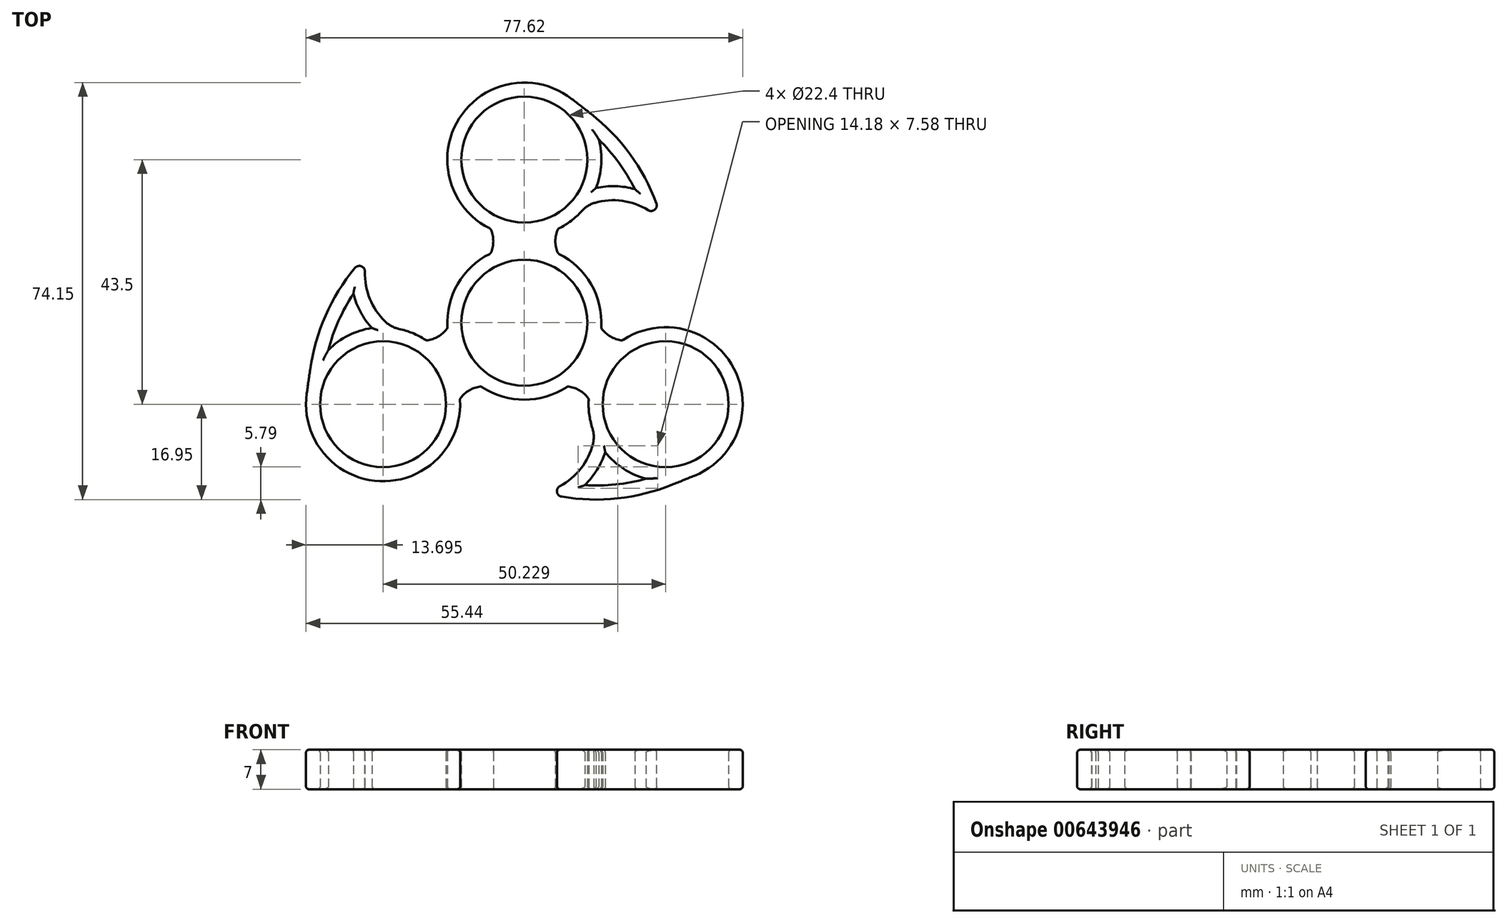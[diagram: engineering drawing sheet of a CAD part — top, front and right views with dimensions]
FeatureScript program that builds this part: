
annotation { "Feature Type Name" : "Feature", "Feature Type Description" : "" }
export const myFeature = defineFeature(function(context is Context, id is Id, definition is map)
    precondition{}
    {
        {
            var Q0;
            Q0=qCreatedBy(makeId("Top.planeOp"),FACE);
            var sketch = newSketch(context, id + "F0", { "sketchPlane" : qUnion([Q0])});
            skCircle(sketch, "E0", {"center": v(0, 0) * mm, "radius": 11.2 * mm});
            skLineSegment(sketch, "E1", {"start": v(0, 0) * mm, "end": v(0, 29) * mm, "construction": true});
            skCircle(sketch, "E2", {"center": v(0, 29) * mm, "radius": 11.2 * mm});
            skLineSegment(sketch, "E3", {"start": v(-11.2, 0) * mm, "end": v(11.2, 0) * mm, "construction": true});
            skLineSegment(sketch, "E4", {"start": v(-11.2, 29) * mm, "end": v(11.2, 29) * mm, "construction": true});
            skArc(sketch, "E5.0", {"start": v(-6, 12.32) * mm, "mid": v(0, -13.7) * mm, "end": v(6, 12.32) * mm});
            skLineSegment(sketch, "E6", {"start": v(0, 42.7) * mm, "end": v(0, 15.3) * mm, "construction": true});
            skLineSegment(sketch, "E7.0", {"start": v(6, 9.46) * mm, "end": v(6, 19.54) * mm, "construction": true});
            skArc(sketch, "E8", {"start": v(6, 16.68) * mm, "mid": v(5.52, 14.5) * mm, "end": v(6, 12.32) * mm});
            skArc(sketch, "E9.MirrorCS", {"start": v(-6, 16.68) * mm, "mid": v(-5.52, 14.5) * mm, "end": v(-6, 12.32) * mm});
            skArc(sketch, "E10.trimOffspring", {"start": v(6, 16.68) * mm, "mid": v(8.7, 18.4) * mm, "end": v(10.9, 20.71) * mm});
            skArc(sketch, "E11", {"start": v(24.52, 17.91) * mm, "mid": v(19, 29.66) * mm, "end": v(9.67, 38.7) * mm});
            skArc(sketch, "E12", {"start": v(24.52, 17.91) * mm, "mid": v(18.17, 21.54) * mm, "end": v(10.9, 20.71) * mm});
            skArc(sketch, "E13.0", {"start": v(19.65, 23.75) * mm, "mid": v(16.2, 24.27) * mm, "end": v(12.73, 23.95) * mm});
            skArc(sketch, "E13.1", {"start": v(19.65, 23.75) * mm, "mid": v(16.8, 28.44) * mm, "end": v(13.22, 32.6) * mm});
            skArc(sketch, "E14.trimOffspring", {"start": v(9.67, 38.7) * mm, "mid": v(-11.16, 36.94) * mm, "end": v(-6, 16.68) * mm});
            skArc(sketch, "E15.trimOffspring", {"start": v(12.73, 23.95) * mm, "mid": v(13.68, 28.23) * mm, "end": v(13.22, 32.6) * mm});
            skSolve(sketch);
        }
        {
            var Q0;
            Q0=makeQuery(id+"F0.imprint","IMPRINT",FACE,{"disambiguationData":[TD([[makeQuery(id+"F0.imprint","IMPRINT",EDGE,{"derivedFrom":sQuery(id+"F0.wireOp",EDGE,"E0")}),-1.0]])]});
            extrude(context, id + "F1", {"entities" : qUnion([Q0]), "depth" : 7 * mm, "offsetDistance" : 25 * mm});
        }
        {
            var Q0;
            Q0=qCreatedBy(makeId("Right.planeOp"),FACE);
            var sketch = newSketch(context, id + "F2", { "sketchPlane" : qUnion([Q0])});
            skLineSegment(sketch, "E16", {"start": v(0, 0) * mm, "end": v(0, 24.15) * mm, "construction": true});
            skSolve(sketch);
        }
        {
            var Q0;
            Q0=makeQuery(id+"F1.opExtrude","SWEPT_EDGE",EDGE,{"disambiguationData":[OSD([sQuery(id+"F0.wireOp",EDGE,"E11"),sQuery(id+"F0.wireOp",EDGE,"E12")])]});
            fillet(context, id + "F3", {"entities" : qUnion([Q0]), "radius" : 1 * mm, "tangentPropagation" : true, "allowEdgeOverflow" : false});
        }
        {
            var Q0;
            Q0=makeQuery(id+"F1.opExtrude","SWEPT_EDGE",EDGE,{"disambiguationData":[OSD([sQuery(id+"F0.wireOp",EDGE,"E10.trimOffspring"),sQuery(id+"F0.wireOp",EDGE,"E12")])]});
            fillet(context, id + "F4", {"entities" : qUnion([Q0]), "radius" : 5 * mm, "tangentPropagation" : true, "allowEdgeOverflow" : false});
        }
        {
            var Q0;
            Q0=makeQuery(id+"F1.opExtrude","SWEPT_EDGE",EDGE,{"disambiguationData":[OSD([sQuery(id+"F0.wireOp",EDGE,"E8"),sQuery(id+"F0.wireOp",EDGE,"a7715e3d-49e1-4b64-8228-6264ce36ffdd.trimOffspring")])]});
            var Q1;
            Q1=makeQuery(id+"F1.opExtrude","SWEPT_EDGE",EDGE,{"disambiguationData":[OSD([sQuery(id+"F0.wireOp",EDGE,"vL0yK9kr-aUAw-fq5m-LhdP-4na97wzfjfiJ"),sQuery(id+"F0.wireOp",EDGE,"a7715e3d-49e1-4b64-8228-6264ce36ffdd.trimOffspring")])]});
            var Q2;
            Q2=makeQuery(id+"F1.opExtrude","SWEPT_EDGE",EDGE,{"disambiguationData":[OSD([sQuery(id+"F0.wireOp",EDGE,"0uLAjghk-3gFu-Hscj-w9fE-ttjJYeJmuMDI"),sQuery(id+"F0.wireOp",EDGE,"vL0yK9kr-aUAw-fq5m-LhdP-4na97wzfjfiJ")])]});
            var Q3;
            Q3=makeQuery(id+"F1.opExtrude","SWEPT_EDGE",EDGE,{"disambiguationData":[OSD([sQuery(id+"F0.wireOp",EDGE,"59cc2289-ca77-47a6-96da-44b8b7f5bab30.MirrorCS"),sQuery(id+"F0.wireOp",EDGE,"5cff57ee-30ec-4a3f-ae05-e4d68d5af566.0")])]});
            var Q4;
            Q4=makeQuery(id+"F1.opExtrude","SWEPT_EDGE",EDGE,{"disambiguationData":[OSD([sQuery(id+"F0.wireOp",EDGE,"Nf5N08YX-LUpC-YIFK-iieG-ll9huf0In2a7"),sQuery(id+"F0.wireOp",EDGE,"59cc2289-ca77-47a6-96da-44b8b7f5bab30.MirrorCS")])]});
            var Q5;
            Q5=makeQuery(id+"F1.opExtrude","SWEPT_EDGE",EDGE,{"disambiguationData":[OSD([sQuery(id+"F0.wireOp",EDGE,"Nf5N08YX-LUpC-YIFK-iieG-ll9huf0In2a7"),sQuery(id+"F0.wireOp",EDGE,"8e5a45cd-34c5-40eb-b1f5-600c90d6d9e0.0")])]});
            var Q6;
            Q6=makeQuery(id+"F1.opExtrude","SWEPT_EDGE",EDGE,{"disambiguationData":[OSD([sQuery(id+"F0.wireOp",EDGE,"8e5a45cd-34c5-40eb-b1f5-600c90d6d9e0.0"),sQuery(id+"F0.wireOp",EDGE,"5cff57ee-30ec-4a3f-ae05-e4d68d5af566.0")])]});
            var Q7;
            Q7=makeQuery(id+"F1.opExtrude","SWEPT_EDGE",EDGE,{"disambiguationData":[OSD([sQuery(id+"F0.wireOp",EDGE,"E9.MirrorCS"),sQuery(id+"F0.wireOp",EDGE,"E14.trimOffspring")])]});
            var Q8;
            Q8=makeQuery(id+"F1.opExtrude","SWEPT_EDGE",EDGE,{"disambiguationData":[OSD([sQuery(id+"F0.wireOp",EDGE,"E5.0"),sQuery(id+"F0.wireOp",EDGE,"E9.MirrorCS")])]});
            fillet(context, id + "F5", {"entities" : qUnion([Q0, Q1, Q2, Q3, Q4, Q5, Q6, Q7, Q8]), "radius" : 0.5 * mm, "tangentPropagation" : true, "allowEdgeOverflow" : false});
        }
        {
            var Q0;
            Q0=makeQuery(id+"F1.opExtrude","SWEPT_EDGE",EDGE,{"disambiguationData":[OSD([sQuery(id+"F0.wireOp",EDGE,"E11"),sQuery(id+"F0.wireOp",EDGE,"E14.trimOffspring")])]});
            fillet(context, id + "F6", {"entities" : qUnion([Q0]), "radius" : 1952.43 * mm, "tangentPropagation" : true, "allowEdgeOverflow" : false});
        }
        {
            var Q0;
            Q0=makeQuery(id+"F1.opExtrude","SWEPT_BODY",BODY,{"disambiguationData":[OSD([sQuery(id+"F0.wireOp",EDGE,"E0"),sQuery(id+"F0.wireOp",EDGE,"E2"),sQuery(id+"F0.wireOp",EDGE,"E5.0"),sQuery(id+"F0.wireOp",EDGE,"beef2716-db7f-41ab-9648-4623db96a248.0"),sQuery(id+"F0.wireOp",EDGE,"0uLAjghk-3gFu-Hscj-w9fE-ttjJYeJmuMDI"),sQuery(id+"F0.wireOp",EDGE,"vL0yK9kr-aUAw-fq5m-LhdP-4na97wzfjfiJ"),sQuery(id+"F0.wireOp",EDGE,"c7e23209-4e23-4cac-a964-1c74d8cbfa74.0"),sQuery(id+"F0.wireOp",EDGE,"c7e23209-4e23-4cac-a964-1c74d8cbfa74.1"),sQuery(id+"F0.wireOp",EDGE,"df6599d3-b23b-4a78-9647-52215b223935.trimOffspring"),sQuery(id+"F0.wireOp",EDGE,"E8"),sQuery(id+"F0.wireOp",EDGE,"E9.MirrorCS"),sQuery(id+"F0.wireOp",EDGE,"7884432a-9f31-4921-b3fb-1dd42b4fd2c3.0"),sQuery(id+"F0.wireOp",EDGE,"36360b40-f322-41f0-b5ba-529e4c97dfdc.0"),sQuery(id+"F0.wireOp",EDGE,"c7395060-edcf-4106-a591-bdadd866a779.0"),sQuery(id+"F0.wireOp",EDGE,"68ec89d5-ddd9-4a57-ad5e-668f128be303.0"),sQuery(id+"F0.wireOp",EDGE,"a7715e3d-49e1-4b64-8228-6264ce36ffdd.trimOffspring")])]});
            var Q1;
            Q1=sQuery(id+"F2.wireOp",EDGE,"E16");
            circularPattern(context, id + "F7", {"operationType" : NewBodyOperationType.ADD, "entities" : qUnion([Q0]), "axis" : qUnion([Q1]), "angle" : 360 * degree, "instanceCount" : 3, "equalSpace" : true});
        }
        {
            var Q0;
            {var subQ0=makeQuery(id+"F1.opExtrude","CAP_FACE",FACE,{"disambiguationData":[OSD([sQuery(id+"F0.wireOp",EDGE,"E0"),sQuery(id+"F0.wireOp",EDGE,"E2"),sQuery(id+"F0.wireOp",EDGE,"E5.0"),sQuery(id+"F0.wireOp",EDGE,"E8"),sQuery(id+"F0.wireOp",EDGE,"E9.MirrorCS"),sQuery(id+"F0.wireOp",EDGE,"Nf5N08YX-LUpC-YIFK-iieG-ll9huf0In2a7"),sQuery(id+"F0.wireOp",EDGE,"8e5a45cd-34c5-40eb-b1f5-600c90d6d9e0.0"),sQuery(id+"F0.wireOp",EDGE,"59cc2289-ca77-47a6-96da-44b8b7f5bab30.MirrorCS"),sQuery(id+"F0.wireOp",EDGE,"5cff57ee-30ec-4a3f-ae05-e4d68d5af566.0"),sQuery(id+"F0.wireOp",EDGE,"E10.trimOffspring"),sQuery(id+"F0.wireOp",EDGE,"E11"),sQuery(id+"F0.wireOp",EDGE,"E12"),sQuery(id+"F0.wireOp",EDGE,"E13.0"),sQuery(id+"F0.wireOp",EDGE,"E13.1"),sQuery(id+"F0.wireOp",EDGE,"E14.trimOffspring"),sQuery(id+"F0.wireOp",EDGE,"E15.trimOffspring")])],"isStart":false});Q0=makeQuery(id+"F7.boolean.opBoolean","MERGE",FACE,{"derivedFrom":[subQ0,makeQuery(id+"F7.opPattern","COPY",FACE,{"derivedFrom":subQ0,"instanceName":"1"}),makeQuery(id+"F7.opPattern","COPY",FACE,{"derivedFrom":subQ0,"instanceName":"2"})]});}
            var Q1;
            {var subQ0=makeQuery(id+"F1.opExtrude","CAP_FACE",FACE,{"disambiguationData":[OSD([sQuery(id+"F0.wireOp",EDGE,"E0"),sQuery(id+"F0.wireOp",EDGE,"E2"),sQuery(id+"F0.wireOp",EDGE,"E5.0"),sQuery(id+"F0.wireOp",EDGE,"E8"),sQuery(id+"F0.wireOp",EDGE,"E9.MirrorCS"),sQuery(id+"F0.wireOp",EDGE,"Nf5N08YX-LUpC-YIFK-iieG-ll9huf0In2a7"),sQuery(id+"F0.wireOp",EDGE,"8e5a45cd-34c5-40eb-b1f5-600c90d6d9e0.0"),sQuery(id+"F0.wireOp",EDGE,"59cc2289-ca77-47a6-96da-44b8b7f5bab30.MirrorCS"),sQuery(id+"F0.wireOp",EDGE,"5cff57ee-30ec-4a3f-ae05-e4d68d5af566.0"),sQuery(id+"F0.wireOp",EDGE,"E10.trimOffspring"),sQuery(id+"F0.wireOp",EDGE,"E11"),sQuery(id+"F0.wireOp",EDGE,"E12"),sQuery(id+"F0.wireOp",EDGE,"E13.0"),sQuery(id+"F0.wireOp",EDGE,"E13.1"),sQuery(id+"F0.wireOp",EDGE,"E14.trimOffspring"),sQuery(id+"F0.wireOp",EDGE,"E15.trimOffspring")])],"isStart":true});Q1=makeQuery(id+"F7.boolean.opBoolean","MERGE",FACE,{"derivedFrom":[subQ0,makeQuery(id+"F7.opPattern","COPY",FACE,{"derivedFrom":subQ0,"instanceName":"1"}),makeQuery(id+"F7.opPattern","COPY",FACE,{"derivedFrom":subQ0,"instanceName":"2"})]});}
            fillet(context, id + "F8", {"entities" : qUnion([Q0, Q1]), "radius" : 0.5 * mm, "tangentPropagation" : true, "allowEdgeOverflow" : false});
        }
    });
